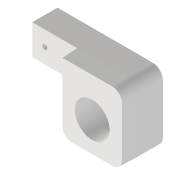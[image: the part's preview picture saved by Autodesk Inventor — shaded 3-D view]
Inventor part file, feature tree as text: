
AUTODESK INVENTOR PART (.ipt)
format: ipt  version: 2022 (Build 260153000, 153)  size: 107,008 bytes
history: native  units: mm
features: other x3, reference x2, extrude x1, sketch x1
ambient origin geometry x8: Origin, YZ Plane, XZ Plane, XY Plane, X Axis, Y Axis, Z Axis, Center Point
bodies: Volumenkörper1 (feature_tree)
feature tree (7):
  extrude  "Extrusion1"  Depth=5.0mm
  sketch  "Skizze1"  dims[d0=6.0mm d1=5.0mm d2=6.0mm d3=2.0mm d4=5.0mm d5=0.0mm d9=2.0mm d10=6.7mm]
  reference  "Referenz1"
  reference  "Referenz2"
  other  "Baugruppe1"
  other  "00_Microlinearmotor:1"
  other  "IM_Lensholder_motorized:1"
